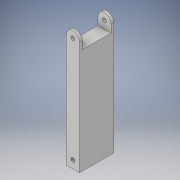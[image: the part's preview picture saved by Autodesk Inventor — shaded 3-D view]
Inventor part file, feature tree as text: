
AUTODESK INVENTOR PART (.ipt)
format: ipt  version: 2019 (Build 230136000, 136)  size: 128,512 bytes
history: native  units: mm
features: extrude x4, sketch x4, other x1
ambient origin geometry x8: Origin, YZ Plane, XZ Plane, XY Plane, X Axis, Y Axis, Z Axis, Center Point
bodies: Body1 (feature_tree)
feature tree (9):
  other  "Sólido1"
  extrude  "Extrusión1"  Depth=130.0mm
  extrude  "Extrusión2"  Depth=400.0mm
  extrude  "Extrusión3"  Depth=15.0mm
  extrude  "Extrusión4"  Depth=10.0mm TaperAngle=0.0deg
  sketch  "Boceto1"  dims[d0=50.0mm d1=130.0mm]
  sketch  "Boceto2"  dims[d2=400.0mm d3=0.0mm d4=30.0mm]
  sketch  "Boceto3"  dims[d5=30.0mm d6=15.0mm]
  sketch  "Boceto4"  dims[d7=10.0mm d8=0.0mm d9=10.0mm d10=0.0mm d11=30.0mm d12=15.0mm d13=10.0mm d14=0.0mm]
